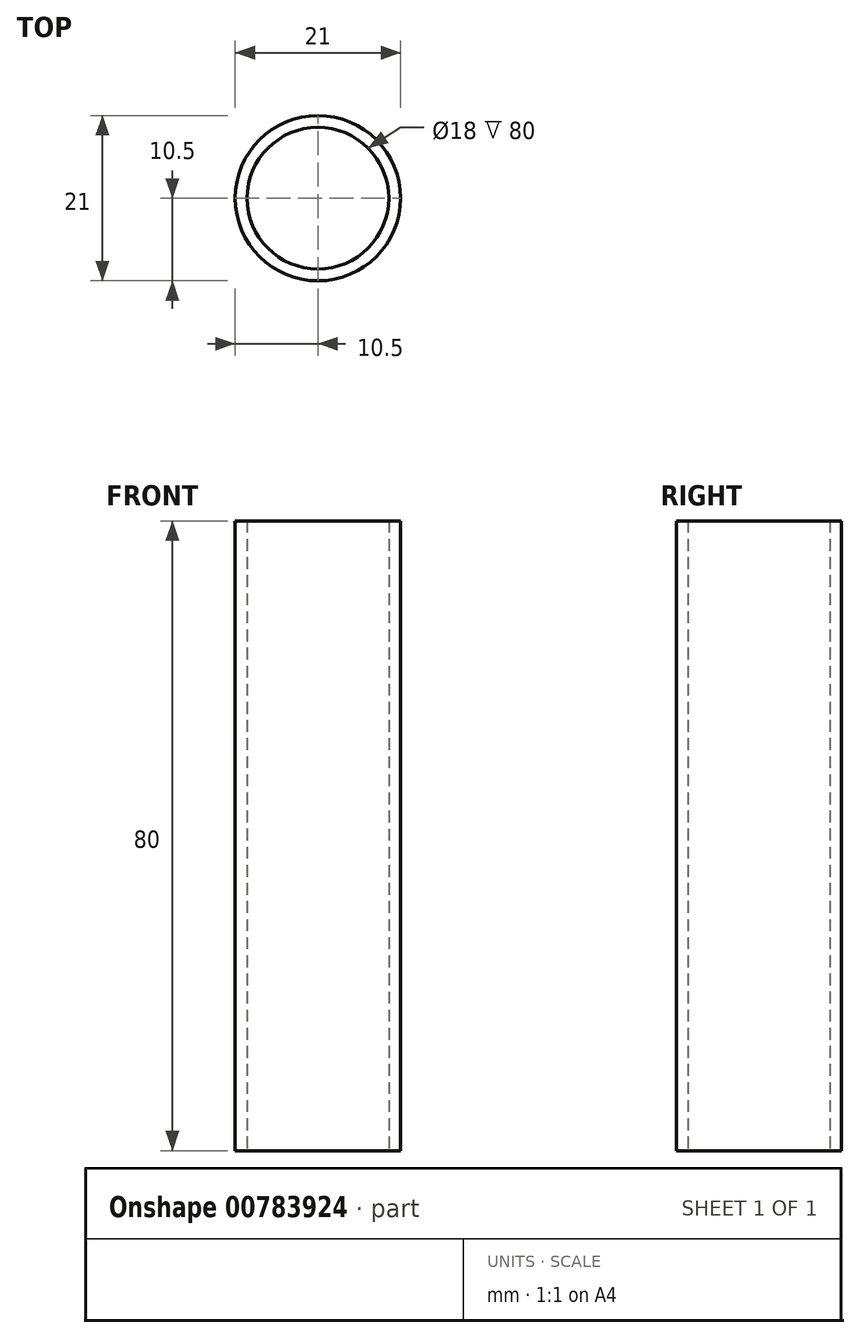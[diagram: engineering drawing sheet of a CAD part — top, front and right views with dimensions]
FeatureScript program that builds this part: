
annotation { "Feature Type Name" : "Feature", "Feature Type Description" : "" }
export const myFeature = defineFeature(function(context is Context, id is Id, definition is map)
    precondition{}
    {
        {
            var Q0;
            Q0=qCreatedBy(makeId("Top.planeOp"),FACE);
            var sketch = newSketch(context, id + "F0", { "sketchPlane" : qUnion([Q0])});
            skCircle(sketch, "E0", {"center": v(0, 0) * mm, "radius": 10.5 * mm});
            skCircle(sketch, "E1", {"center": v(0, 0) * mm, "radius": 9 * mm});
            skSolve(sketch);
        }
        {
            var Q0;
            Q0=makeQuery(id+"F0.imprint","IMPRINT",FACE,{"disambiguationData":[TD([[makeQuery(id+"F0.imprint","IMPRINT",EDGE,{"derivedFrom":sQuery(id+"F0.wireOp",EDGE,"E0")}),1.0]])]});
            extrude(context, id + "F1", {"entities" : qUnion([Q0]), "depth" : 80 * mm, "offsetDistance" : 25.4 * mm});
        }
    });
